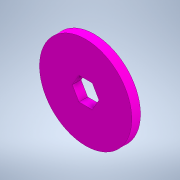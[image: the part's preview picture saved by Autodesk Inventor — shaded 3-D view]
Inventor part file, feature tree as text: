
AUTODESK INVENTOR PART (.ipt)
format: ipt  version: 2021.2 (Build 252289000, 289)  size: 104,960 bytes
history: native  units: in
note: dims shown in document units (in); Inventor stores cm internally (conversion verified against a paired STEP export)
features: extrude x1, sketch x1
ambient origin geometry x8: Origin, YZ Plane, XZ Plane, XY Plane, X Axis, Y Axis, Z Axis, Center Point
bodies: Solid1 (feature_tree)
feature tree (2):
  extrude  "Extrusion1"  Depth=0.1875in
  sketch  "Sketch1"  dims[d0=0.5in d2=2.0in d3=0.7113in d4=0.1875in d5=0.0in]
